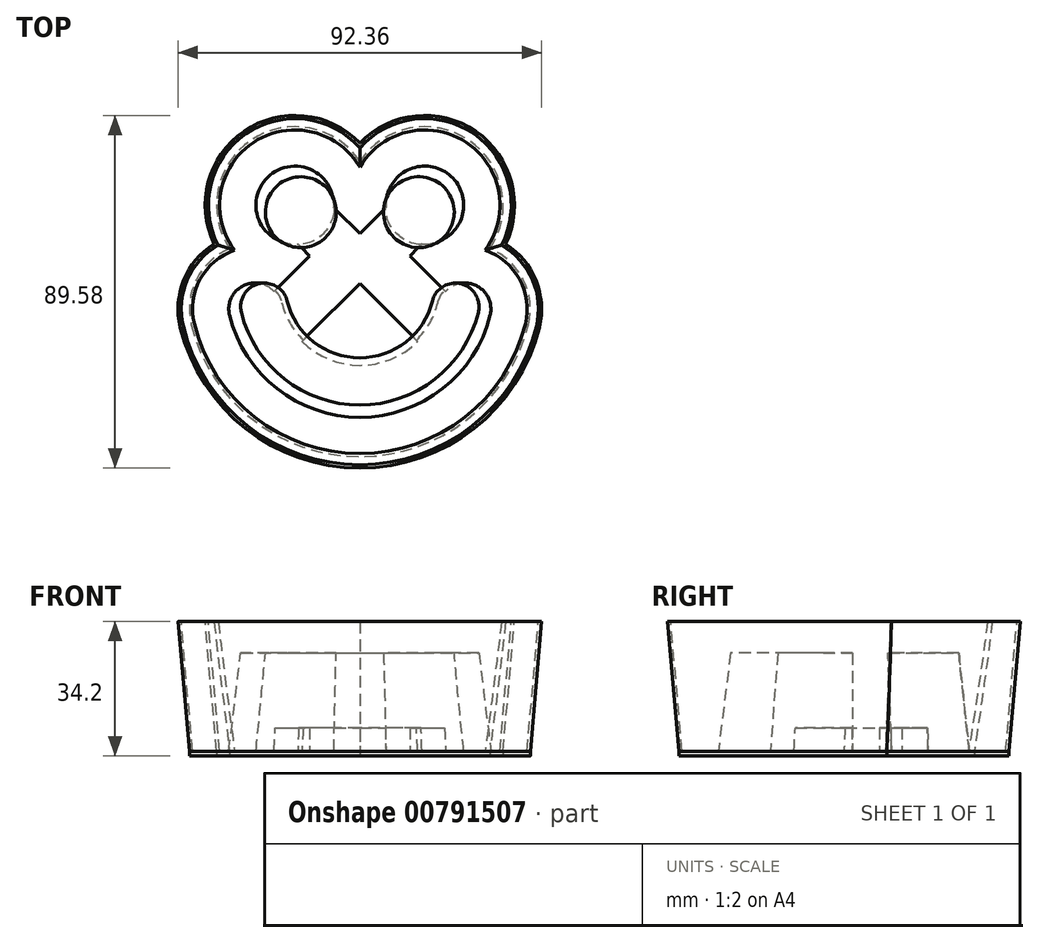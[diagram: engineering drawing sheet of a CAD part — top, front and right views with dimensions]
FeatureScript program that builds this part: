
annotation { "Feature Type Name" : "Feature", "Feature Type Description" : "" }
export const myFeature = defineFeature(function(context is Context, id is Id, definition is map)
    precondition{}
    {
        {
            var Q0;
            Q0=qCreatedBy(makeId("Top.planeOp"),FACE);
            var sketch = newSketch(context, id + "F0", { "sketchPlane" : qUnion([Q0])});
            skCircle(sketch, "E0", {"center": v(15, 18) * mm, "radius": 9 * mm});
            skCircle(sketch, "E1", {"center": v(-15, 18) * mm, "radius": 9 * mm});
            skArc(sketch, "E2", {"start": v(30.1, -7.44) * mm, "mid": v(25.7, -0.18) * mm, "end": v(18.44, -4.56) * mm});
            skArc(sketch, "E3", {"start": v(-18.44, -4.56) * mm, "mid": v(-25.7, -0.18) * mm, "end": v(-30.1, -7.44) * mm});
            skArc(sketch, "E4", {"start": v(-30.1, -7.44) * mm, "mid": v(0, -31) * mm, "end": v(30.1, -7.44) * mm});
            skArc(sketch, "E5", {"start": v(-18.44, -4.56) * mm, "mid": v(0, -19) * mm, "end": v(18.44, -4.56) * mm});
            skLineSegment(sketch, "E6", {"start": v(-43.32, -6) * mm, "end": v(59.83, -6) * mm, "construction": true});
            skLineSegment(sketch, "E7", {"start": v(0, 39) * mm, "end": v(0, -57.45) * mm, "construction": true});
            skLineSegment(sketch, "E8", {"start": v(-50.54, 18) * mm, "end": v(62.86, 18) * mm, "construction": true});
            skCircle(sketch, "E9", {"center": v(0, 0) * mm, "radius": 30 * mm, "construction": true});
            skSolve(sketch);
        }
        {
            var Q0;
            Q0=qCreatedBy(makeId("Top.planeOp"),FACE);
            cPlane(context, id + "F1", {"entities" : qUnion([Q0]), "cplaneType" : CPlaneType.OFFSET, "offset" : 25 * mm, "oppositeDirection" : true, "width" : 150 * mm, "height" : 150 * mm});
        }
        {
            var Q0;
            Q0=qCreatedBy(id+"F1.planeOp",FACE);
            var sketch = newSketch(context, id + "F2", { "sketchPlane" : qUnion([Q0])});
            skArc(sketch, "E10.0", {"start": v(-18.44, -4.56) * mm, "mid": v(-25.7, -0.18) * mm, "end": v(-30.1, -7.44) * mm});
            skArc(sketch, "E10.1", {"start": v(-30.1, -7.44) * mm, "mid": v(0, -31) * mm, "end": v(30.1, -7.44) * mm});
            skArc(sketch, "E10.2", {"start": v(-18.44, -4.56) * mm, "mid": v(0, -19) * mm, "end": v(18.44, -4.56) * mm});
            skCircle(sketch, "E10.3", {"center": v(15, 18) * mm, "radius": 9 * mm});
            skCircle(sketch, "E10.4", {"center": v(-15, 18) * mm, "radius": 9 * mm});
            skArc(sketch, "E10.5", {"start": v(30.1, -7.44) * mm, "mid": v(25.7, -0.18) * mm, "end": v(18.44, -4.56) * mm});
            skSolve(sketch);
        }
        {
            var Q0;
            Q0 = qSketchRegion(id + "F2", true);
            extrude(context, id + "F3", {"entities" : qUnion([Q0]), "oppositeDirection" : true, "depth" : 0.1 * mm, "offsetDistance" : 25 * mm});
        }
        {
            var Q0;
            Q0=makeQuery(id+"F3.opExtrude","SWEPT_BODY",BODY,{"disambiguationData":[OSD([sQuery(id+"F2.wireOp",EDGE,"E10.4")])]});
            var Q1;
            Q1=makeQuery(id+"F3.opExtrude","SWEPT_BODY",BODY,{"disambiguationData":[OSD([sQuery(id+"F2.wireOp",EDGE,"E10.3")])]});
            var Q2;
            Q2=makeQuery(id+"F3.opExtrude","SWEPT_BODY",BODY,{"disambiguationData":[OSD([sQuery(id+"F2.wireOp",EDGE,"E10.0"),sQuery(id+"F2.wireOp",EDGE,"E10.1"),sQuery(id+"F2.wireOp",EDGE,"E10.2"),sQuery(id+"F2.wireOp",EDGE,"E10.5")])]});
            var Q3;
            Q3=sQuery(id+"F2.wireOp",VERTEX,"E10.2.center");
            transform(context, id + "F4", {"entities" : qUnion([Q0, Q1, Q2]), "transformType" : TransformType.SCALE_UNIFORMLY, "scale" : 1.1, "scalePoint" : qUnion([Q3]), "makeCopy" : false});
        }
        {
            var Q0;
            Q0=qCreatedBy(id+"F1.planeOp",FACE);
            var sketch = newSketch(context, id + "F5", { "sketchPlane" : qUnion([Q0])});
            skCircle(sketch, "E11.0", {"center": v(-16.5, 19.8) * mm, "radius": 9.9 * mm});
            skArc(sketch, "E12.0", {"start": v(-20.29, -5.02) * mm, "mid": v(-28.28, -0.2) * mm, "end": v(-33.1, -8.18) * mm});
            skArc(sketch, "E13.0", {"start": v(-33.1, -8.18) * mm, "mid": v(0, -34.1) * mm, "end": v(33.1, -8.18) * mm});
            skArc(sketch, "E14.0", {"start": v(-20.29, -5.02) * mm, "mid": v(0, -20.9) * mm, "end": v(20.29, -5.02) * mm});
            skArc(sketch, "E15.0", {"start": v(33.1, -8.18) * mm, "mid": v(28.28, -0.2) * mm, "end": v(20.29, -5.02) * mm});
            skCircle(sketch, "E16.0", {"center": v(16.5, 19.8) * mm, "radius": 9.9 * mm});
            skSolve(sketch);
        }
        {
            var Q0;
            Q0=qCreatedBy(id+"F1.planeOp",FACE);
            var sketch = newSketch(context, id + "F6", { "sketchPlane" : qUnion([Q0])});
            skArc(sketch, "E17.0", {"start": v(33.04, 8.74) * mm, "mid": v(27.6, 36.32) * mm, "end": v(0, 30.92) * mm});
            skArc(sketch, "E18.0", {"start": v(0, 30.92) * mm, "mid": v(-27.6, 36.32) * mm, "end": v(-33.04, 8.74) * mm});
            skArc(sketch, "E19.0", {"start": v(42.81, -10.58) * mm, "mid": v(41.51, 0.89) * mm, "end": v(33.04, 8.74) * mm});
            skArc(sketch, "E19.1", {"start": v(-42.81, -10.58) * mm, "mid": v(0, -44.1) * mm, "end": v(42.81, -10.58) * mm});
            skArc(sketch, "E19.2", {"start": v(-33.04, 8.74) * mm, "mid": v(-41.51, 0.89) * mm, "end": v(-42.81, -10.58) * mm});
            skSolve(sketch);
        }
        {
            var Q0;
            Q0 = qSketchRegion(id + "F6", true);
            extrude(context, id + "F7", {"entities" : qUnion([Q0]), "depth" : 33 * mm, "offsetDistance" : 25 * mm, "hasDraft" : true, "draftAngle" : 5 * degree, "hasSecondDirection" : true, "secondDirectionOppositeDirection" : true, "secondDirectionDepth" : 0.8 * mm});
        }
        {
            var Q0;
            Q0=makeQuery(id+"F7.opExtrude","CAP_FACE",FACE,{"disambiguationData":[OSD([sQuery(id+"F6.wireOp",EDGE,"E17.0"),sQuery(id+"F6.wireOp",EDGE,"E18.0"),sQuery(id+"F6.wireOp",EDGE,"E19.0"),sQuery(id+"F6.wireOp",EDGE,"E19.1"),sQuery(id+"F6.wireOp",EDGE,"E19.2")])],"isStart":false});
            shell(context, id + "F8", {"entities" : qUnion([Q0]), "thickness" : 0.8 * mm});
        }
        {
            var Q0;
            Q0=makeQuery(id+"F7.opExtrude","CAP_FACE",FACE,{"disambiguationData":[OSD([sQuery(id+"F6.wireOp",EDGE,"E17.0"),sQuery(id+"F6.wireOp",EDGE,"E18.0"),sQuery(id+"F6.wireOp",EDGE,"E19.0"),sQuery(id+"F6.wireOp",EDGE,"E19.1"),sQuery(id+"F6.wireOp",EDGE,"E19.2")])],"isStart":true});
            extrude(context, id + "F9", {"entities" : qUnion([Q0]), "operationType" : NewBodyOperationType.ADD, "depth" : 0.4 * mm, "offsetDistance" : 25 * mm});
        }
        {
            var Q0;
            Q0=sQuery(id+"F6.wireOp",VERTEX,"E18.0.center");
            var Q1;
            Q1=sQuery(id+"F0.wireOp",VERTEX,"E1.center");
            var Q2;
            Q2=sQuery(id+"F0.wireOp",VERTEX,"E0.center");
            cPlane(context, id + "F10", {"entities" : qUnion([Q0, Q1, Q2]), "cplaneType" : CPlaneType.THREE_POINT, "offset" : 25 * mm, "width" : 150 * mm, "height" : 150 * mm});
        }
        {
            var Q0;
            Q0=sQuery(id+"F6.wireOp",VERTEX,"E19.2.center");
            var Q1;
            Q1=sQuery(id+"F0.wireOp",VERTEX,"E3.center");
            var Q2;
            Q2=sQuery(id+"F6.wireOp",VERTEX,"E19.0.center");
            cPlane(context, id + "F11", {"entities" : qUnion([Q0, Q1, Q2]), "cplaneType" : CPlaneType.THREE_POINT, "offset" : 25 * mm, "width" : 150 * mm, "height" : 150 * mm});
        }
        {
            var Q1;
            Q1=makeQuery(id+"F0.imprint","IMPRINT",FACE,{"disambiguationData":[TD([[makeQuery(id+"F0.imprint","IMPRINT",EDGE,{"derivedFrom":sQuery(id+"F0.wireOp",EDGE,"E1")}),1.0]])]});
            var Q2;
            Q2=makeQuery(id+"F5.imprint","IMPRINT",FACE,{"disambiguationData":[TD([[makeQuery(id+"F5.imprint","IMPRINT",EDGE,{"derivedFrom":sQuery(id+"F5.wireOp",EDGE,"E11.0")}),1.0]])]});
            loft(context, id + "F12", {"operationType" : NewBodyOperationType.ADD, "sheetProfilesArray" : [{ "sheetProfileEntities" : qUnion([Q1]) }, { "sheetProfileEntities" : qUnion([Q2]) }]});
        }
        {
            var Q1;
            Q1=makeQuery(id+"F0.imprint","IMPRINT",FACE,{"disambiguationData":[TD([[makeQuery(id+"F0.imprint","IMPRINT",EDGE,{"derivedFrom":sQuery(id+"F0.wireOp",EDGE,"E0")}),1.0]])]});
            var Q2;
            Q2=makeQuery(id+"F5.imprint","IMPRINT",FACE,{"disambiguationData":[TD([[makeQuery(id+"F5.imprint","IMPRINT",EDGE,{"derivedFrom":sQuery(id+"F5.wireOp",EDGE,"E16.0")}),1.0]])]});
            loft(context, id + "F13", {"operationType" : NewBodyOperationType.ADD, "sheetProfilesArray" : [{ "sheetProfileEntities" : qUnion([Q1]) }, { "sheetProfileEntities" : qUnion([Q2]) }]});
        }
        {
            var Q1;
            Q1=makeQuery(id+"F5.imprint","IMPRINT",FACE,{"disambiguationData":[TD([[makeQuery(id+"F5.imprint","IMPRINT",EDGE,{"derivedFrom":sQuery(id+"F5.wireOp",EDGE,"E12.0")}),1.0]])]});
            var Q2;
            Q2=makeQuery(id+"F0.imprint","IMPRINT",FACE,{"disambiguationData":[TD([[makeQuery(id+"F0.imprint","IMPRINT",EDGE,{"derivedFrom":sQuery(id+"F0.wireOp",EDGE,"E2")}),1.0]])]});
            loft(context, id + "F14", {"operationType" : NewBodyOperationType.ADD, "sheetProfilesArray" : [{ "sheetProfileEntities" : qUnion([Q1]) }, { "sheetProfileEntities" : qUnion([Q2]) }]});
        }
        {
            var Q0;
            Q0=qCreatedBy(id+"F1.planeOp",FACE);
            var sketch = newSketch(context, id + "F15", { "sketchPlane" : qUnion([Q0])});
            skLineSegment(sketch, "E20", {"start": v(-10.6, 23.17) * mm, "end": v(0, 12.56) * mm});
            skLineSegment(sketch, "E21", {"start": v(0, 12.56) * mm, "end": v(10.6, 23.17) * mm});
            skLineSegment(sketch, "E22", {"start": v(10.6, 23.17) * mm, "end": v(19.8, 13.98) * mm});
            skLineSegment(sketch, "E23", {"start": v(19.8, 13.98) * mm, "end": v(12.73, 6.9) * mm});
            skLineSegment(sketch, "E24", {"start": v(12.73, 6.9) * mm, "end": v(27.58, -7.94) * mm});
            skLineSegment(sketch, "E25", {"start": v(17.68, -17.84) * mm, "end": v(0, -0.17) * mm});
            skLineSegment(sketch, "E26", {"start": v(0, -0.17) * mm, "end": v(-17.68, -17.84) * mm});
            skLineSegment(sketch, "E27", {"start": v(-27.58, -7.94) * mm, "end": v(-12.73, 6.9) * mm});
            skLineSegment(sketch, "E28", {"start": v(-12.73, 6.9) * mm, "end": v(-19.8, 13.98) * mm});
            skLineSegment(sketch, "E29", {"start": v(-19.8, 13.98) * mm, "end": v(-10.6, 23.17) * mm});
            skLineSegment(sketch, "E30", {"start": v(-27.58, -7.94) * mm, "end": v(-17.68, -17.84) * mm});
            skLineSegment(sketch, "E31", {"start": v(17.68, -17.84) * mm, "end": v(27.58, -7.94) * mm});
            skSolve(sketch);
        }
        {
            var Q0;
            Q0=makeQuery(id+"F15.imprint","IMPRINT",FACE,{"disambiguationData":[TD([[makeQuery(id+"F15.imprint","IMPRINT",EDGE,{"derivedFrom":sQuery(id+"F15.wireOp",EDGE,"E20")}),-1.0]])]});
            extrude(context, id + "F16", {"entities" : qUnion([Q0]), "operationType" : NewBodyOperationType.ADD, "depth" : 6 * mm, "offsetDistance" : 25 * mm});
        }
    });
